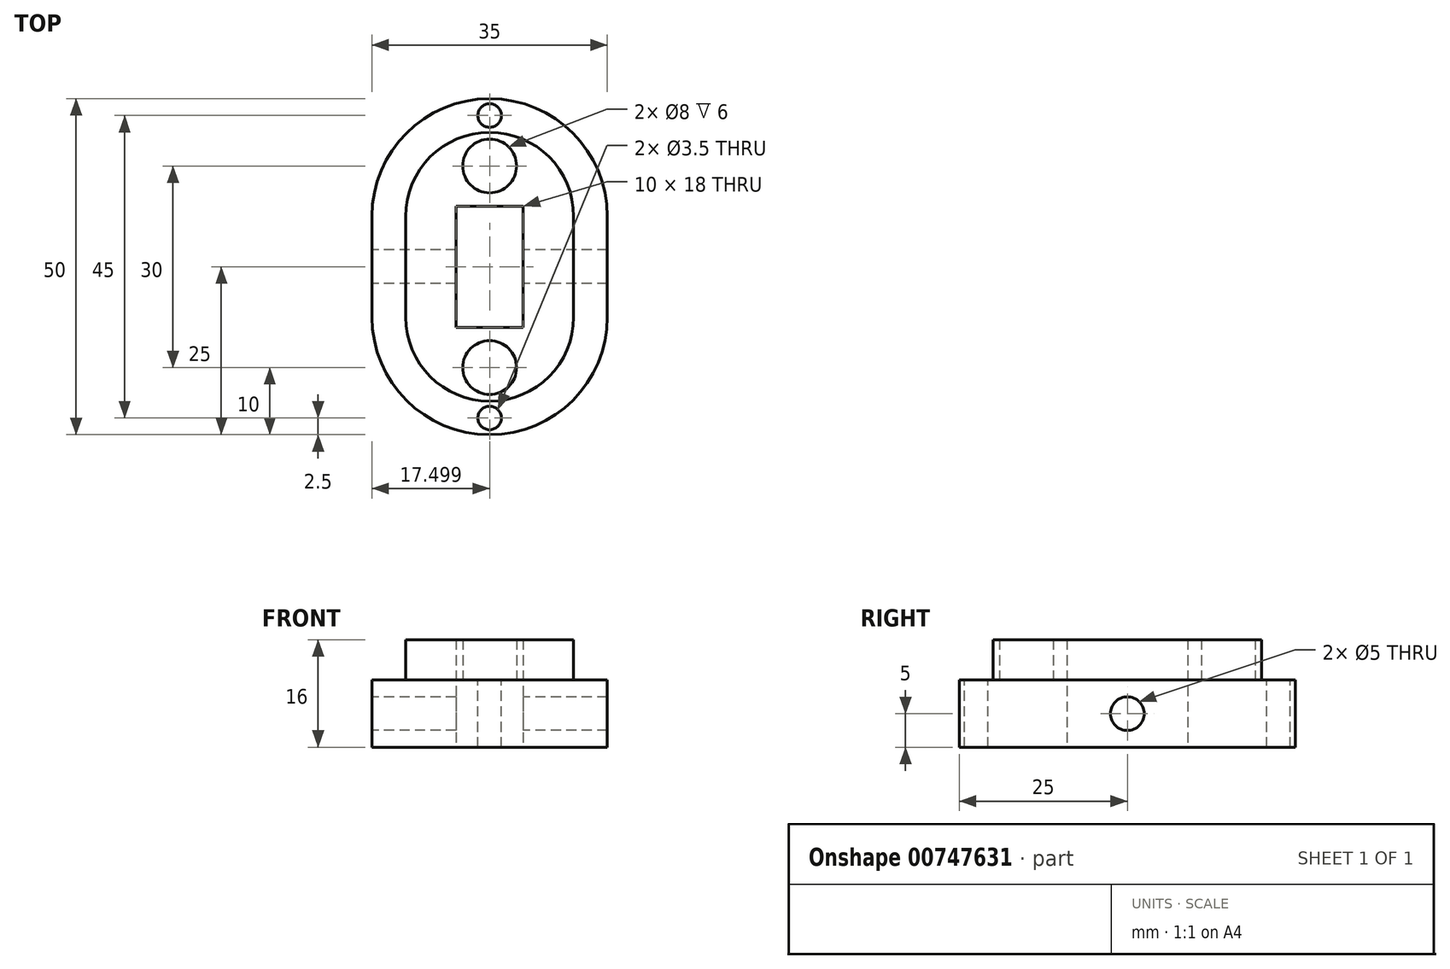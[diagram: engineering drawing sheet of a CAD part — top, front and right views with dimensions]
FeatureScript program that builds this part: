
annotation { "Feature Type Name" : "Feature", "Feature Type Description" : "" }
export const myFeature = defineFeature(function(context is Context, id is Id, definition is map)
    precondition{}
    {
        {
            var Q0;
            Q0=qCreatedBy(makeId("Top.planeOp"),FACE);
            var sketch = newSketch(context, id + "F0", { "sketchPlane" : qUnion([Q0])});
            skLineSegment(sketch, "E0.bottom", {"start": v(-47.16, 15) * mm, "end": v(-22.16, 15) * mm});
            skLineSegment(sketch, "E0.top", {"start": v(-47.16, 0) * mm, "end": v(-22.16, 0) * mm});
            skLineSegment(sketch, "E0.left", {"start": v(-47.16, 15) * mm, "end": v(-47.16, 0) * mm});
            skLineSegment(sketch, "E0.right", {"start": v(-22.16, 15) * mm, "end": v(-22.16, 0) * mm});
            skArc(sketch, "E1", {"start": v(-22.16, 15) * mm, "mid": v(-34.66, 27.5) * mm, "end": v(-47.16, 15) * mm});
            skArc(sketch, "E2", {"start": v(-47.16, 0) * mm, "mid": v(-34.66, -12.5) * mm, "end": v(-22.16, 0) * mm});
            skSolve(sketch);
        }
        {
            var Q0;
            Q0 = qSketchRegion(id + "F0", true);
            extrude(context, id + "F1", {"entities" : qUnion([Q0]), "depth" : 6 * mm, "offsetDistance" : 25.4 * mm});
        }
        {
            var Q0;
            Q0=qCreatedBy(makeId("Top.planeOp"),FACE);
            var sketch = newSketch(context, id + "F2", { "sketchPlane" : qUnion([Q0])});
            skArc(sketch, "E3.0", {"start": v(-17.16, 15) * mm, "mid": v(-34.66, 32.5) * mm, "end": v(-52.16, 15) * mm});
            skLineSegment(sketch, "E3.1", {"start": v(-17.16, 15) * mm, "end": v(-17.16, 0) * mm});
            skArc(sketch, "E3.2", {"start": v(-52.16, 0) * mm, "mid": v(-34.66, -17.5) * mm, "end": v(-17.16, 0) * mm});
            skLineSegment(sketch, "E3.3", {"start": v(-52.16, 15) * mm, "end": v(-52.16, 0) * mm});
            skSolve(sketch);
        }
        {
            var Q0;
            Q0=makeQuery(id+"F2.imprint","IMPRINT",FACE,{"disambiguationData":[TD([[makeQuery(id+"F2.imprint","IMPRINT",EDGE,{"derivedFrom":sQuery(id+"F2.wireOp",EDGE,"E3.0")}),1.0]])]});
            extrude(context, id + "F3", {"entities" : qUnion([Q0]), "operationType" : NewBodyOperationType.ADD, "oppositeDirection" : true, "depth" : 10 * mm, "offsetDistance" : 25.4 * mm});
        }
        {
            var Q0;
            Q0=makeQuery(id+"F3.opExtrude","SWEPT_FACE",FACE,{"disambiguationData":[OSD([sQuery(id+"F2.wireOp",EDGE,"E3.3")])]});
            var sketch = newSketch(context, id + "F4", { "sketchPlane" : qUnion([Q0])});
            skPoint(sketch, "E4", {"position": v(-7.5, -5) * mm});
            skLineSegment(sketch, "E5", {"start": v(-7.5, -5) * mm, "end": v(-15, 0) * mm, "construction": true});
            skLineSegment(sketch, "E6", {"start": v(-7.5, -5) * mm, "end": v(0, -10) * mm, "construction": true});
            skLineSegment(sketch, "E7", {"start": v(-7.5, -5) * mm, "end": v(0, 0) * mm, "construction": true});
            skLineSegment(sketch, "E8", {"start": v(-7.5, -5) * mm, "end": v(-15, -10) * mm, "construction": true});
            skSolve(sketch);
        }
        {
            var Q0;
            Q0=sQuery(id+"F4.wireOp",VERTEX,"E4");
            var Q1;
            Q1=makeQuery(id+"F1.opExtrude","SWEPT_BODY",BODY,{"disambiguationData":[OSD([sQuery(id+"F0.wireOp",EDGE,"E0.left"),sQuery(id+"F0.wireOp",EDGE,"E0.right"),sQuery(id+"F0.wireOp",EDGE,"E1"),sQuery(id+"F0.wireOp",EDGE,"E2")])]});
            hole(context, id + "F5", {"style" : HoleStyle.SIMPLE, "endStyle" : HoleEndStyle.THROUGH, "holeDiameter" : 5 * mm, "majorDiameter" : 6.35 * mm, "isTappedThrough" : true, "tappedDepth" : 12.7 * mm, "tapClearance" : 3, "locations" : qUnion([Q0]), "scope" : qUnion([Q1])});
        }
        {
            var Q0;
            Q0=makeQuery(id+"F3.opExtrude","CAP_FACE",FACE,{"disambiguationData":[OSD([sQuery(id+"F2.wireOp",EDGE,"E3.0"),sQuery(id+"F2.wireOp",EDGE,"E3.1"),sQuery(id+"F2.wireOp",EDGE,"E3.2"),sQuery(id+"F2.wireOp",EDGE,"E3.3")])],"isStart":false});
            var sketch = newSketch(context, id + "F6", { "sketchPlane" : qUnion([Q0])});
            skLineSegment(sketch, "E9", {"start": v(-52.16, 0) * mm, "end": v(-17.16, 0) * mm});
            skLineSegment(sketch, "E10", {"start": v(-17.16, -15) * mm, "end": v(-52.16, -15) * mm});
            skLineSegment(sketch, "E11.bottom", {"start": v(-39.66, 1.5) * mm, "end": v(-29.66, 1.5) * mm});
            skLineSegment(sketch, "E11.top", {"start": v(-39.66, -16.5) * mm, "end": v(-29.66, -16.5) * mm});
            skLineSegment(sketch, "E11.left", {"start": v(-39.66, 1.5) * mm, "end": v(-39.66, -16.5) * mm});
            skLineSegment(sketch, "E11.right", {"start": v(-29.66, 1.5) * mm, "end": v(-29.66, -16.5) * mm});
            skLineSegment(sketch, "E12", {"start": v(-39.66, 1.5) * mm, "end": v(-52.16, 0) * mm, "construction": true});
            skLineSegment(sketch, "E13", {"start": v(-52.16, -15) * mm, "end": v(-39.66, -16.5) * mm, "construction": true});
            skLineSegment(sketch, "E14", {"start": v(-29.66, -16.5) * mm, "end": v(-17.16, -15) * mm, "construction": true});
            skLineSegment(sketch, "E15", {"start": v(-29.66, 1.5) * mm, "end": v(-17.16, 0) * mm, "construction": true});
            skCircle(sketch, "E16", {"center": v(-34.66, -22.5) * mm, "radius": 4 * mm});
            skCircle(sketch, "E17", {"center": v(-34.66, 7.5) * mm, "radius": 4 * mm});
            skLineSegment(sketch, "E18", {"start": v(-34.66, -22.5) * mm, "end": v(-34.66, -16.5) * mm});
            skLineSegment(sketch, "E19", {"start": v(-34.66, 7.5) * mm, "end": v(-34.66, 1.5) * mm});
            skSolve(sketch);
        }
        {
            var Q0;
            {var subQ0=sQuery(id+"F6.wireOp",EDGE,"E11.left");var subQ1=sQuery(id+"F6.wireOp",EDGE,"E9");var subQ2=makeQuery(id+"F6.imprint","INTERSECT",VERTEX,{"derivedFrom":[subQ1,subQ0]});Q0=makeQuery(id+"F6.imprint","IMPRINT",FACE,{"disambiguationData":[TD([[makeQuery(id+"F6.imprint","IMPRINT",EDGE,{"disambiguationData":[TD([[subQ2,-1.0]])],"derivedFrom":subQ1}),-1.0]])]});}
            var Q1;
            {var subQ1=sQuery(id+"F6.wireOp",EDGE,"E11.top");var subQ5=makeQuery(id+"F6.imprint","IMPRINT",VERTEX,{"derivedFrom":subQ1});Q1=makeQuery(id+"F6.imprint","IMPRINT",FACE,{"disambiguationData":[TD([[makeQuery(id+"F6.imprint","IMPRINT",EDGE,{"disambiguationData":[TD([[subQ5,1.0]])],"derivedFrom":subQ1}),1.0]])]});}
            var Q2;
            {var subQ1=sQuery(id+"F6.wireOp",EDGE,"E11.bottom");var subQ7=makeQuery(id+"F6.imprint","IMPRINT",VERTEX,{"derivedFrom":subQ1});Q2=makeQuery(id+"F6.imprint","IMPRINT",FACE,{"disambiguationData":[TD([[makeQuery(id+"F6.imprint","IMPRINT",EDGE,{"disambiguationData":[TD([[subQ7,1.0]])],"derivedFrom":subQ1}),-1.0]])]});}
            var Q3;
            Q3=makeQuery(id+"F1.opExtrude","CAP_FACE",FACE,{"disambiguationData":[OSD([sQuery(id+"F0.wireOp",EDGE,"E0.left"),sQuery(id+"F0.wireOp",EDGE,"E0.right"),sQuery(id+"F0.wireOp",EDGE,"E1"),sQuery(id+"F0.wireOp",EDGE,"E2")])],"isStart":false});
            extrude(context, id + "F7", {"entities" : qUnion([Q0, Q1, Q2]), "operationType" : NewBodyOperationType.REMOVE, "endBound" : BoundingType.UP_TO_SURFACE, "oppositeDirection" : true, "depth" : 25.4 * mm, "endBoundEntityFace" : qUnion([Q3]), "offsetDistance" : 25.4 * mm});
        }
        {
            var Q0;
            Q0=makeQuery(id+"F6.imprint","IMPRINT",FACE,{"disambiguationData":[TD([[makeQuery(id+"F6.imprint","IMPRINT",EDGE,{"derivedFrom":sQuery(id+"F6.wireOp",EDGE,"E16")}),1.0]])]});
            var Q1;
            Q1=makeQuery(id+"F6.imprint","IMPRINT",FACE,{"disambiguationData":[TD([[makeQuery(id+"F6.imprint","IMPRINT",EDGE,{"derivedFrom":sQuery(id+"F6.wireOp",EDGE,"E17")}),1.0]])]});
            extrude(context, id + "F8", {"entities" : qUnion([Q0, Q1]), "operationType" : NewBodyOperationType.REMOVE, "oppositeDirection" : true, "depth" : 25.4 * mm, "offsetDistance" : 25.4 * mm});
        }
        {
            var Q0;
            Q0=makeQuery(id+"F6.imprint","IMPRINT",FACE,{"disambiguationData":[TD([[makeQuery(id+"F6.imprint","IMPRINT",EDGE,{"derivedFrom":sQuery(id+"F6.wireOp",EDGE,"E16")}),1.0]])]});
            var Q1;
            Q1=makeQuery(id+"F6.imprint","IMPRINT",FACE,{"disambiguationData":[TD([[makeQuery(id+"F6.imprint","IMPRINT",EDGE,{"derivedFrom":sQuery(id+"F6.wireOp",EDGE,"E17")}),1.0]])]});
            extrude(context, id + "F9", {"entities" : qUnion([Q0, Q1]), "operationType" : NewBodyOperationType.ADD, "oppositeDirection" : true, "depth" : 10 * mm, "offsetDistance" : 25.4 * mm});
        }
        {
            var Q0;
            Q0=makeQuery(id+"F3.opExtrude","CAP_FACE",FACE,{"disambiguationData":[OSD([sQuery(id+"F2.wireOp",EDGE,"E3.0"),sQuery(id+"F2.wireOp",EDGE,"E3.1"),sQuery(id+"F2.wireOp",EDGE,"E3.2"),sQuery(id+"F2.wireOp",EDGE,"E3.3")])],"isStart":true});
            var sketch = newSketch(context, id + "F10", { "sketchPlane" : qUnion([Q0])});
            skCircle(sketch, "E20", {"center": v(-34.66, 30) * mm, "radius": 1.75 * mm});
            skPoint(sketch, "E20.centerSnap0", {"position": v(-34.66, 27.5) * mm});
            skCircle(sketch, "E21", {"center": v(-34.66, -15) * mm, "radius": 1.75 * mm});
            skPoint(sketch, "E21.centerSnap0", {"position": v(-34.66, -12.5) * mm});
            skLineSegment(sketch, "E22", {"start": v(-34.66, -12.5) * mm, "end": v(-34.66, -17.5) * mm, "construction": true});
            skLineSegment(sketch, "E23", {"start": v(-34.66, 27.5) * mm, "end": v(-34.66, 32.5) * mm, "construction": true});
            skSolve(sketch);
        }
        {
            var Q0;
            Q0=makeQuery(id+"F10.imprint","IMPRINT",FACE,{"disambiguationData":[TD([[makeQuery(id+"F10.imprint","IMPRINT",EDGE,{"derivedFrom":sQuery(id+"F10.wireOp",EDGE,"E20")}),1.0]])]});
            var Q1;
            Q1=makeQuery(id+"F10.imprint","IMPRINT",FACE,{"disambiguationData":[TD([[makeQuery(id+"F10.imprint","IMPRINT",EDGE,{"derivedFrom":sQuery(id+"F10.wireOp",EDGE,"E21")}),1.0]])]});
            extrude(context, id + "F11", {"entities" : qUnion([Q0, Q1]), "operationType" : NewBodyOperationType.REMOVE, "oppositeDirection" : true, "depth" : 10 * mm, "offsetDistance" : 25 * mm});
        }
    });
